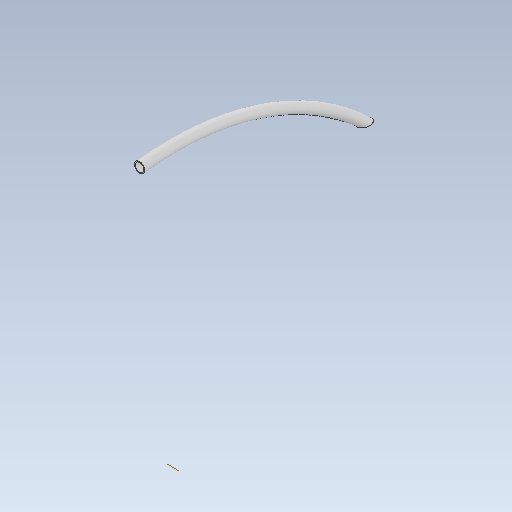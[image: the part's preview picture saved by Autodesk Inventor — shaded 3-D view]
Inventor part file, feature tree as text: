
AUTODESK INVENTOR PART (.ipt)
format: ipt  version: 2021 (Build 250183000, 183)  size: 944,128 bytes
history: native  units: mm
features: sketch x7, extrude x4, sweep x2, pattern_circular x1, fillet x1
ambient origin geometry x8: Origin, YZ Plane, XZ Plane, XY Plane, X Axis, Y Axis, Z Axis, Center Point
bodies: Solid1 (feature_tree)
feature tree (15):
  sketch  "Sketch1"  dims[d0=3300.0mm d1=1650.0mm]
  sweep  "Sweep1"
  sweep  "Sweep2"
  extrude  "Extrusion1"  Depth=50.0mm
  extrude  "Extrusion3"  Depth=1650.0mm
  pattern_circular  "Circular Pattern1"  Count=181  [1 undecoded]
  extrude  "Extrusion5"  Depth=1730.0mm
  extrude  "Extrusion6"  Depth=1730.0mm
  fillet  "Fillet1"  Radius=1730.0mm
  sketch  "Sketch2"  dims[d2=0.0mm d3=60.0mm]
  sketch  "Sketch3"  dims[d4=0.0mm d5=0.0mm d6=50.0mm]
  sketch  "Sketch4"  dims[d7=0.0mm d8=1650.0mm]
  sketch  "Sketch5"  dims[d9=0.0mm d10=0.0mm d11=1810.0mm]
  sketch  "Sketch9"  dims[d12=3460.0mm d13=1730.0mm]
  sketch  "Sketch10"  dims[d14=1200.0mm d15=1730.0mm d16=1730.0mm d17=200.0mm d18=80.0mm d19=0.0mm d20=10.0mm d21=10.0mm d22=0.5mm d25=1.0mm d26=10.0mm d27=0.0mm d28=600.0mm d29=45.0deg d38=10.0mm d39=5.0mm d40=10.0mm d41=0.0mm d42=2.0mm d43=10.0mm d44=0.0mm d45=2.0mm]
note: 1 required parameter value undecoded (feature->parameter linkage not recoverable at this tier; creation-order binding heuristic only, values carry confidence <= 0.55)
